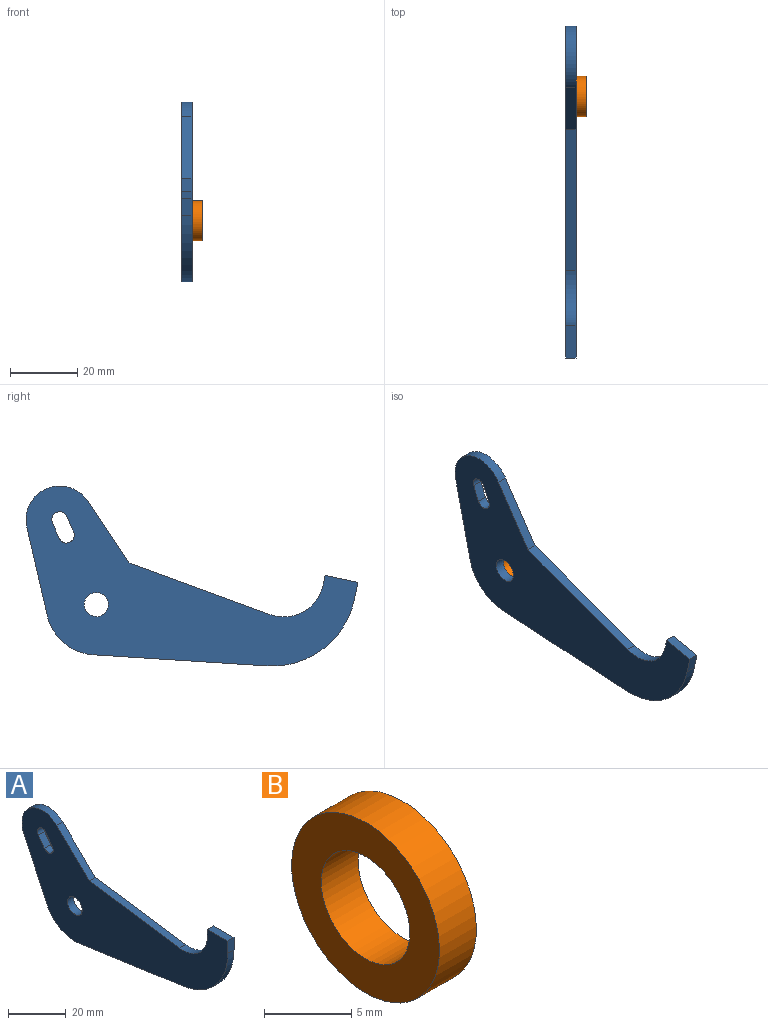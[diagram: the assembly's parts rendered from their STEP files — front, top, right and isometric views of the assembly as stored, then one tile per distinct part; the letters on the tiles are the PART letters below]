
ASSEMBLY  parts=2 mates=1
PART A: 18 faces, bbox 3x101x47.6 mm
  f0: plane 100.95x47.55mm, normal (1,0,0), area 2358.5mm2, adj f1,f2,f3,f4,f5,f6,f7,f8
  f1: cylinder r=2.35mm len=4.27mm, axis (-1,0,0), area 22.1mm2, adj f0,f11,f12,f17
  f2: plane 51.43x7.42mm, normal (0,-0.14,-0.99), area 155.9mm2, adj f0,f3,f10,f17
  f3: cylinder r=15mm len=15.75mm, axis (-1,0,0), area 57.6mm2, adj f0,f2,f4,f17
  f4: plane 24.65x11.41mm, normal (0,0.91,-0.42), area 81.5mm2, adj f0,f3,f5,f17
  f5: cylinder r=10mm len=16.98mm, axis (-1,0,0), area 83.3mm2, adj f0,f4,f6,f17
  f6: plane 15.95x15.56mm, normal (0,-0.7,0.72), area 66.8mm2, adj f0,f5,f7,f17
  f7: plane 44.31x6.4mm, normal (0,-0.14,0.99), area 134.3mm2, adj f0,f6,f8,f17
  f8: cylinder r=12mm len=13.71mm, axis (-1,0,0), area 61.7mm2, adj f0,f7,f9,f17
  f9: plane 3x2.92mm, normal (0,1,0), area 8.8mm2, adj f0,f8,f14,f17
  f10: cylinder r=25mm len=24.74mm, axis (-1,0,0), area 107.1mm2, adj f0,f2,f15,f17
  f11: plane 4.14x3mm, normal (0,-0.82,0.58), area 15.2mm2, adj f0,f1,f13,f17
  f12: plane 4.14x3mm, normal (0,0.82,-0.58), area 15.2mm2, adj f0,f1,f13,f17
  f13: cylinder r=2.35mm len=4.27mm, axis (-1,0,0), area 22.1mm2, adj f0,f11,f12,f17
  f14: plane 10x3mm, normal (0,0,1), area 30mm2, adj f0,f9,f15,f17
  f15: plane 5.23x3mm, normal (0,-1,0), area 15.7mm2, adj f0,f10,f14,f17
  f16: cylinder r=3.6mm len=7.2mm, axis (-1,0,0), area 67.9mm2, adj f0,f17
  f17: plane 100.95x47.55mm, normal (-1,0,0), area 2358.5mm2, adj f1,f2,f3,f4,f5,f6,f7,f8
PART B: 4 faces, bbox 3x12x12 mm
  f0: plane 12x12mm, normal (1,0,0), area 72.4mm2, adj f1,f2
  f1: cylinder r=3.6mm len=7.2mm, axis (-1,0,0), area 67.9mm2, adj f0,f3
  f2: cylinder r=6mm len=12mm, axis (-1,0,0), area 113.1mm2, adj f0,f3
  f3: plane 12x12mm, normal (-1,0,0), area 72.4mm2, adj f1,f2
PLACE A rot(axis=(1,0,0),11.9deg) t=(-44.3,28.47,42.72)mm
PLACE B rot(axis=(1,0,0),11.9deg) t=(-41.3,37.75,-1.41)mm
MATE fastened B.f1 <-> A.f3  axis (-1,0,0) through (-26.3,9.72,15.74)mm
